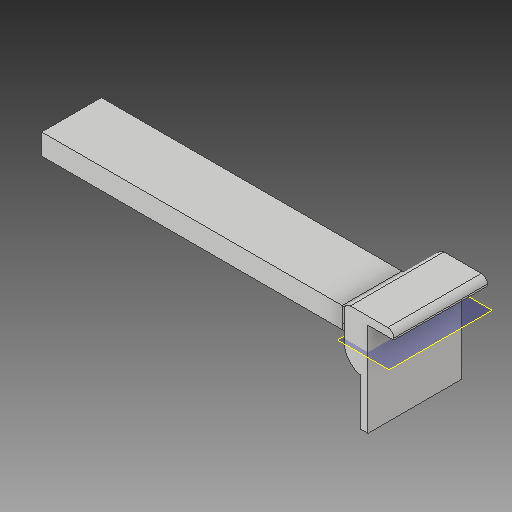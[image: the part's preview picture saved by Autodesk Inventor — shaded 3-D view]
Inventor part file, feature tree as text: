
AUTODESK INVENTOR PART (.ipt)
format: ipt  version: 2018 (Build 220112000, 112)  size: 131,584 bytes
history: native  units: in
note: dims shown in document units (in); Inventor stores cm internally (conversion verified against a paired STEP export)
features: sketch x6, other x3, plane x1
ambient origin geometry x8: Origin, YZ Plane, XZ Plane, XY Plane, X Axis, Y Axis, Z Axis, Center Point
bodies: Solid1 (feature_tree)
feature tree (10):
  other  "straightBar.ipt"
  other  "Solid1::straightBar.ipt"
  other  "TaggingFeature1"
  sketch  "Sketch1"  dims[d0=0.3937in]
  sketch  "Sketch3"
  sketch  "Sketch4"
  sketch  "Sketch5"
  sketch  "Sketch6"
  sketch  "Sketch7"
  plane  "Work Plane1"
